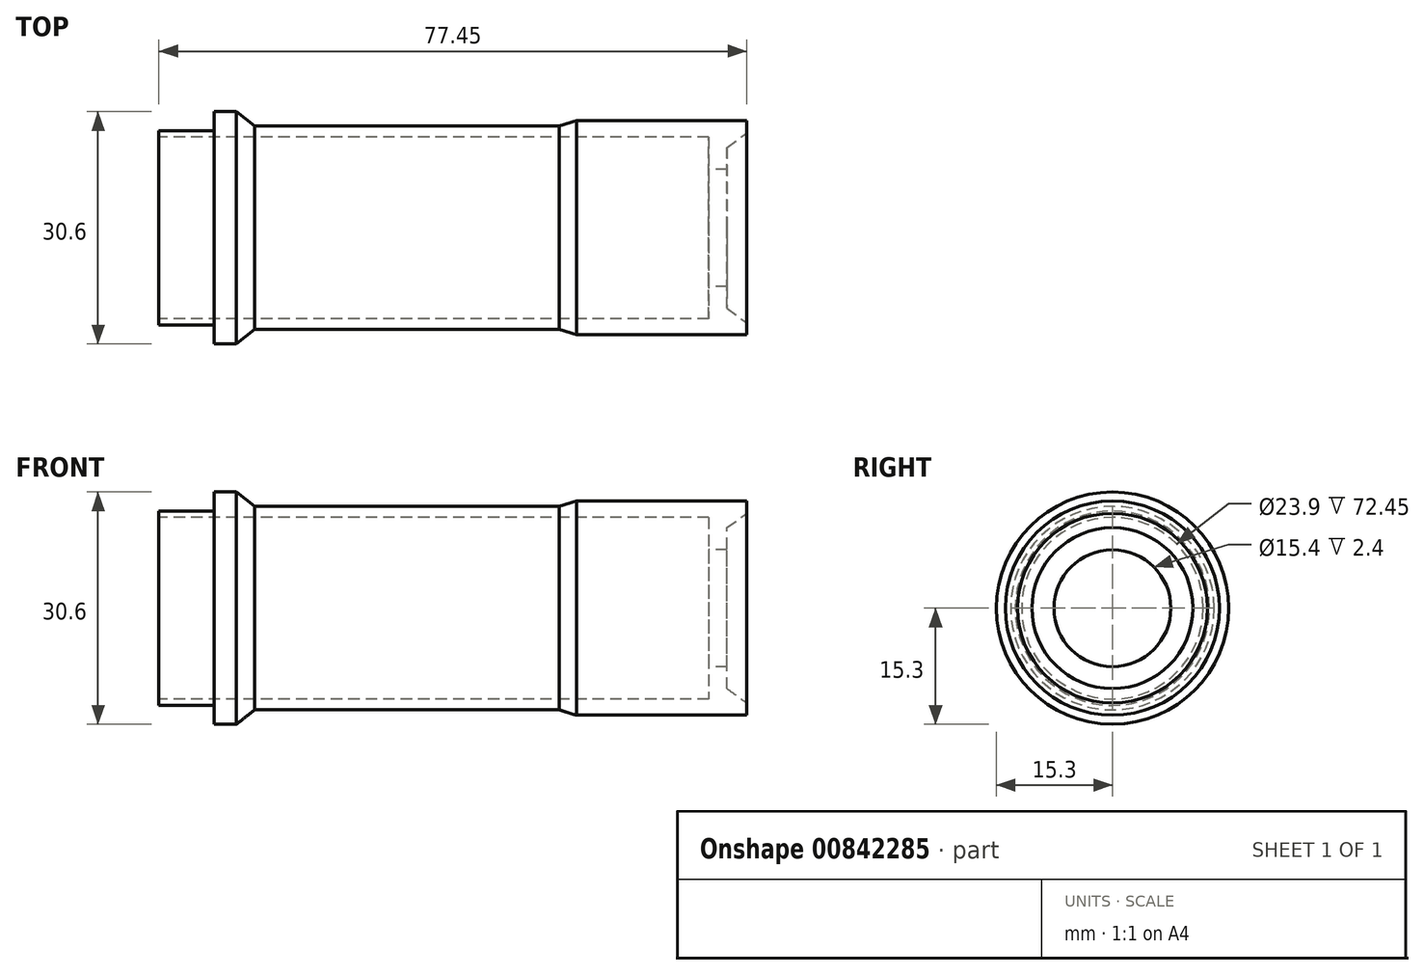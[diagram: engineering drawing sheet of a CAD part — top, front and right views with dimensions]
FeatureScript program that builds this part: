
annotation { "Feature Type Name" : "Feature", "Feature Type Description" : "" }
export const myFeature = defineFeature(function(context is Context, id is Id, definition is map)
    precondition{}
    {
        {
            var Q0;
            Q0=qCreatedBy(makeId("Front.planeOp"),FACE);
            var sketch = newSketch(context, id + "F0", { "sketchPlane" : qUnion([Q0])});
            skLineSegment(sketch, "E0", {"start": v(-34.34, 0) * mm, "end": v(-34.34, 12.8) * mm});
            skLineSegment(sketch, "E1", {"start": v(-34.34, 12.8) * mm, "end": v(-27.04, 12.8) * mm});
            skLineSegment(sketch, "E2", {"start": v(-27.04, 12.8) * mm, "end": v(-27.04, 15.3) * mm});
            skLineSegment(sketch, "E3", {"start": v(-27.04, 15.3) * mm, "end": v(-24.14, 15.3) * mm});
            skLineSegment(sketch, "E4", {"start": v(-24.14, 15.3) * mm, "end": v(-21.74, 13.4) * mm});
            skLineSegment(sketch, "E5", {"start": v(-21.74, 13.4) * mm, "end": v(18.4, 13.4) * mm});
            skLineSegment(sketch, "E6", {"start": v(18.4, 13.4) * mm, "end": v(20.66, 14.1) * mm});
            skLineSegment(sketch, "E7", {"start": v(20.66, 14.1) * mm, "end": v(43.1, 14.1) * mm});
            skLineSegment(sketch, "E8", {"start": v(40.5, 0) * mm, "end": v(-34.34, 0) * mm});
            skLineSegment(sketch, "E9", {"start": v(43.1, 14.1) * mm, "end": v(43.1, 12.5) * mm});
            skLineSegment(sketch, "E10", {"start": v(40.5, 0) * mm, "end": v(40.5, 10.6) * mm});
            skLineSegment(sketch, "E11", {"start": v(40.5, 10.6) * mm, "end": v(43.1, 12.5) * mm});
            skSolve(sketch);
        }
        {
            var Q0;
            Q0=makeQuery(id+"F0.imprint","IMPRINT",FACE,{"disambiguationData":[TD([[makeQuery(id+"F0.imprint","IMPRINT",EDGE,{"derivedFrom":sQuery(id+"F0.wireOp",EDGE,"E0")}),-1.0]])]});
            var Q1;
            Q1=sQuery(id+"F0.wireOp",EDGE,"E8");
            revolve(context, id + "F1", {"surfaceOperationType" : NewSurfaceOperationType.NEW, "entities" : qUnion([Q0]), "axis" : qUnion([Q1]), "revolveType" : RevolveType.FULL});
        }
        {
            var Q0;
            Q0=makeQuery(id+"F1.opRevolve","SWEPT_FACE",FACE,{"disambiguationData":[OSD([sQuery(id+"F0.wireOp",EDGE,"E0")])]});
            var sketch = newSketch(context, id + "F2", { "sketchPlane" : qUnion([Q0])});
            skCircle(sketch, "E12", {"center": v(0, 0) * mm, "radius": 11.95 * mm});
            skSolve(sketch);
        }
        {
            var Q0;
            Q0=makeQuery(id+"F2.imprint","IMPRINT",FACE,{"disambiguationData":[TD([[makeQuery(id+"F2.imprint","IMPRINT",EDGE,{"derivedFrom":sQuery(id+"F2.wireOp",EDGE,"E12")}),1.0]])]});
            extrude(context, id + "F3", {"entities" : qUnion([Q0]), "operationType" : NewBodyOperationType.REMOVE, "oppositeDirection" : true, "depth" : 72.45 * mm, "offsetDistance" : 25 * mm});
        }
        {
            var Q0;
            Q0=makeQuery(id+"F3.boolean.opBoolean","COPY",FACE,{"derivedFrom":makeQuery(id+"F3.opExtrude","CAP_FACE",FACE,{"disambiguationData":[OSD([sQuery(id+"F2.wireOp",EDGE,"E12")])],"isStart":false})});
            var sketch = newSketch(context, id + "F4", { "sketchPlane" : qUnion([Q0])});
            skCircle(sketch, "E13", {"center": v(0, 0) * mm, "radius": 7.7 * mm});
            skSolve(sketch);
        }
        {
            var Q0;
            Q0=makeQuery(id+"F4.imprint","IMPRINT",FACE,{"disambiguationData":[TD([[makeQuery(id+"F4.imprint","IMPRINT",EDGE,{"derivedFrom":sQuery(id+"F4.wireOp",EDGE,"E13")}),1.0]])]});
            extrude(context, id + "F5", {"entities" : qUnion([Q0]), "operationType" : NewBodyOperationType.REMOVE, "endBound" : BoundingType.THROUGH_ALL, "oppositeDirection" : true, "depth" : 25 * mm, "offsetDistance" : 25 * mm});
        }
    });
